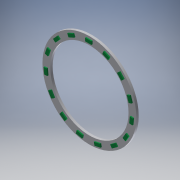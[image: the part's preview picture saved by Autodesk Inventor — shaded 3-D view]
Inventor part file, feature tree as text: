
AUTODESK INVENTOR PART (.ipt)
format: ipt  version: 2017.1 (Build 211199000, 199)  size: 170,496 bytes
history: native  units: mm
features: extrude x2, sketch x2, pattern_circular x1
ambient origin geometry x8: Origin, YZ Plane, XZ Plane, XY Plane, X Axis, Y Axis, Z Axis, Center Point
bodies: Solid1 (feature_tree)
feature tree (5):
  extrude  "Extrusion1"  Depth=50.0mm
  extrude  "Extrusion2"  Depth=2.0mm
  pattern_circular  "Circular Pattern1"  [2 undecoded]
  sketch  "Sketch1"  dims[d0=60.0mm d1=50.0mm]
  sketch  "Sketch2"  dims[d2=1.5mm d3=0.0mm d4=2.0mm d5=26.5mm d6=4.0mm d7=0.75mm d8=0.0mm d9=150.0mm d10=360.0deg]
note: 2 required parameter values undecoded (feature->parameter linkage not recoverable at this tier; creation-order binding heuristic only, values carry confidence <= 0.55)
